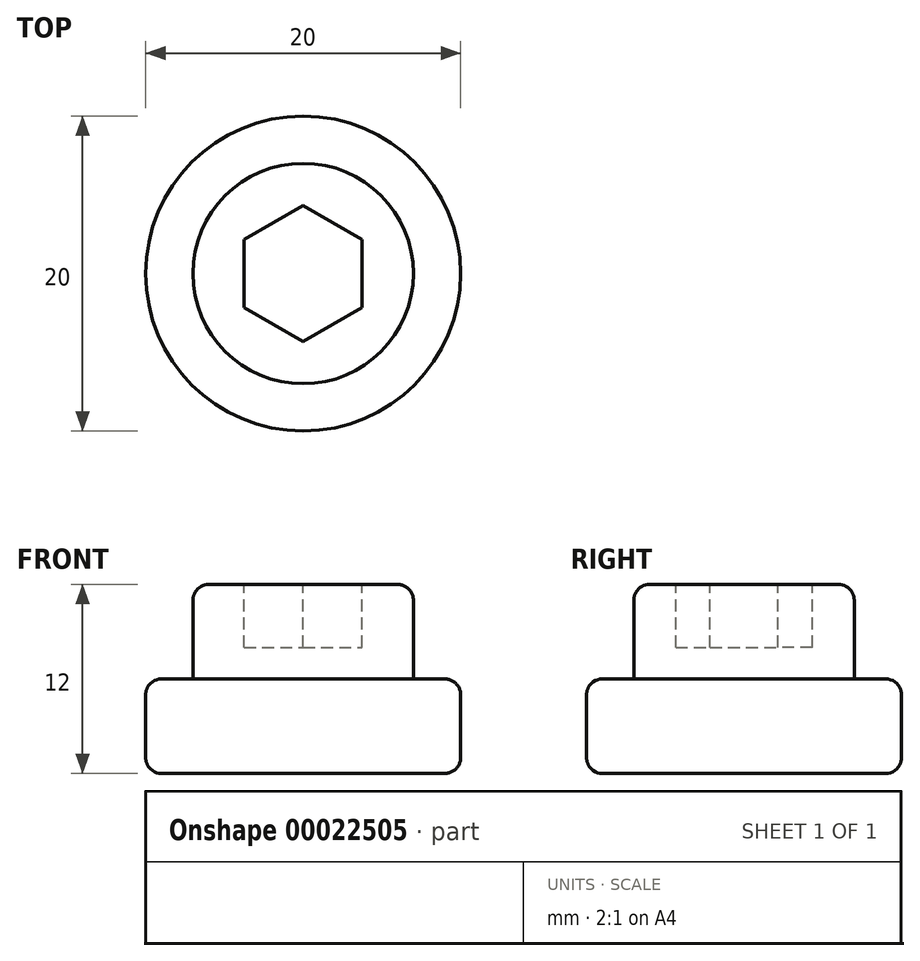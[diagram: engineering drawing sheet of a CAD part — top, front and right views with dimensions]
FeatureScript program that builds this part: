
annotation { "Feature Type Name" : "Feature", "Feature Type Description" : "" }
export const myFeature = defineFeature(function(context is Context, id is Id, definition is map)
    precondition{}
    {
        {
            var Q0;
            Q0=qCreatedBy(makeId("Top.planeOp"),FACE);
            var sketch = newSketch(context, id + "F0", { "sketchPlane" : qUnion([Q0])});
            skCircle(sketch, "E0", {"center": v(0, 0) * mm, "radius": 10 * mm});
            skSolve(sketch);
        }
        {
            var Q0;
            Q0=qSketchRegion(id+"F0",true);
            extrude(context, id + "F1", {"entities" : qUnion([Q0]), "depth" : 6 * mm});
        }
        {
            var Q0;
            Q0=makeQuery(id+"F1.opExtrude","CAP_FACE",FACE,{"disambiguationData":[OSD([sQuery(id+"F0.wireOp",EDGE,"E0")])],"isStart":false});
            var sketch = newSketch(context, id + "F2", { "sketchPlane" : qUnion([Q0])});
            skCircle(sketch, "E1", {"center": v(0, 0) * mm, "radius": 7 * mm});
            skSolve(sketch);
        }
        {
            var Q0;
            Q0=qSketchRegion(id+"F2",true);
            extrude(context, id + "F3", {"entities" : qUnion([Q0]), "operationType" : NewBodyOperationType.ADD, "depth" : 6 * mm});
        }
        {
            var Q0;
            Q0=makeQuery(id+"F3.opExtrude","CAP_FACE",FACE,{"disambiguationData":[OSD([sQuery(id+"F2.wireOp",EDGE,"E1")])],"isStart":false});
            var sketch = newSketch(context, id + "F4", { "sketchPlane" : qUnion([Q0])});
            skCircle(sketch, "E2.cCircle", {"center": v(0, 0) * mm, "radius": 3.75 * mm, "construction": true});
            skLineSegment(sketch, "E2.0", {"start": v(0, 4.33) * mm, "end": v(3.75, 2.17) * mm});
            skLineSegment(sketch, "E2.1", {"start": v(3.75, 2.17) * mm, "end": v(3.75, -2.17) * mm});
            skLineSegment(sketch, "E2.2", {"start": v(3.75, -2.17) * mm, "end": v(0, -4.33) * mm});
            skLineSegment(sketch, "E2.3", {"start": v(0, -4.33) * mm, "end": v(-3.75, -2.17) * mm});
            skLineSegment(sketch, "E2.4", {"start": v(-3.75, -2.17) * mm, "end": v(-3.75, 2.17) * mm});
            skLineSegment(sketch, "E2.5", {"start": v(-3.75, 2.17) * mm, "end": v(0, 4.33) * mm});
            skPoint(sketch, "E2.0.midPoint", {"position": v(1.88, 3.25) * mm});
            skSolve(sketch);
        }
        {
            var Q0;
            Q0=qSketchRegion(id+"F4",true);
            extrude(context, id + "F5", {"entities" : qUnion([Q0]), "operationType" : NewBodyOperationType.REMOVE, "oppositeDirection" : true, "depth" : 4 * mm});
        }
        {
            var Q0;
            Q0=makeQuery(id+"F3.opExtrude","CAP_EDGE",EDGE,{"disambiguationData":[OSD([sQuery(id+"F2.wireOp",EDGE,"E1")])],"isStart":false});
            var Q1;
            Q1=makeQuery(id+"F3.opExtrude","CAP_EDGE",EDGE,{"disambiguationData":[OSD([sQuery(id+"F2.wireOp",EDGE,"E1")])],"isStart":true});
            var Q2;
            Q2=makeQuery(id+"F1.opExtrude","CAP_EDGE",EDGE,{"disambiguationData":[OSD([sQuery(id+"F0.wireOp",EDGE,"E0")])],"isStart":false});
            var Q3;
            Q3=makeQuery(id+"F1.opExtrude","CAP_EDGE",EDGE,{"disambiguationData":[OSD([sQuery(id+"F0.wireOp",EDGE,"E0")])],"isStart":true});
            fillet(context, id + "F6", {"entities" : qUnion([Q0, Q1, Q2, Q3]), "radius" : 1 * mm, "tangentPropagation" : true, "allowEdgeOverflow" : false});
        }
    });
